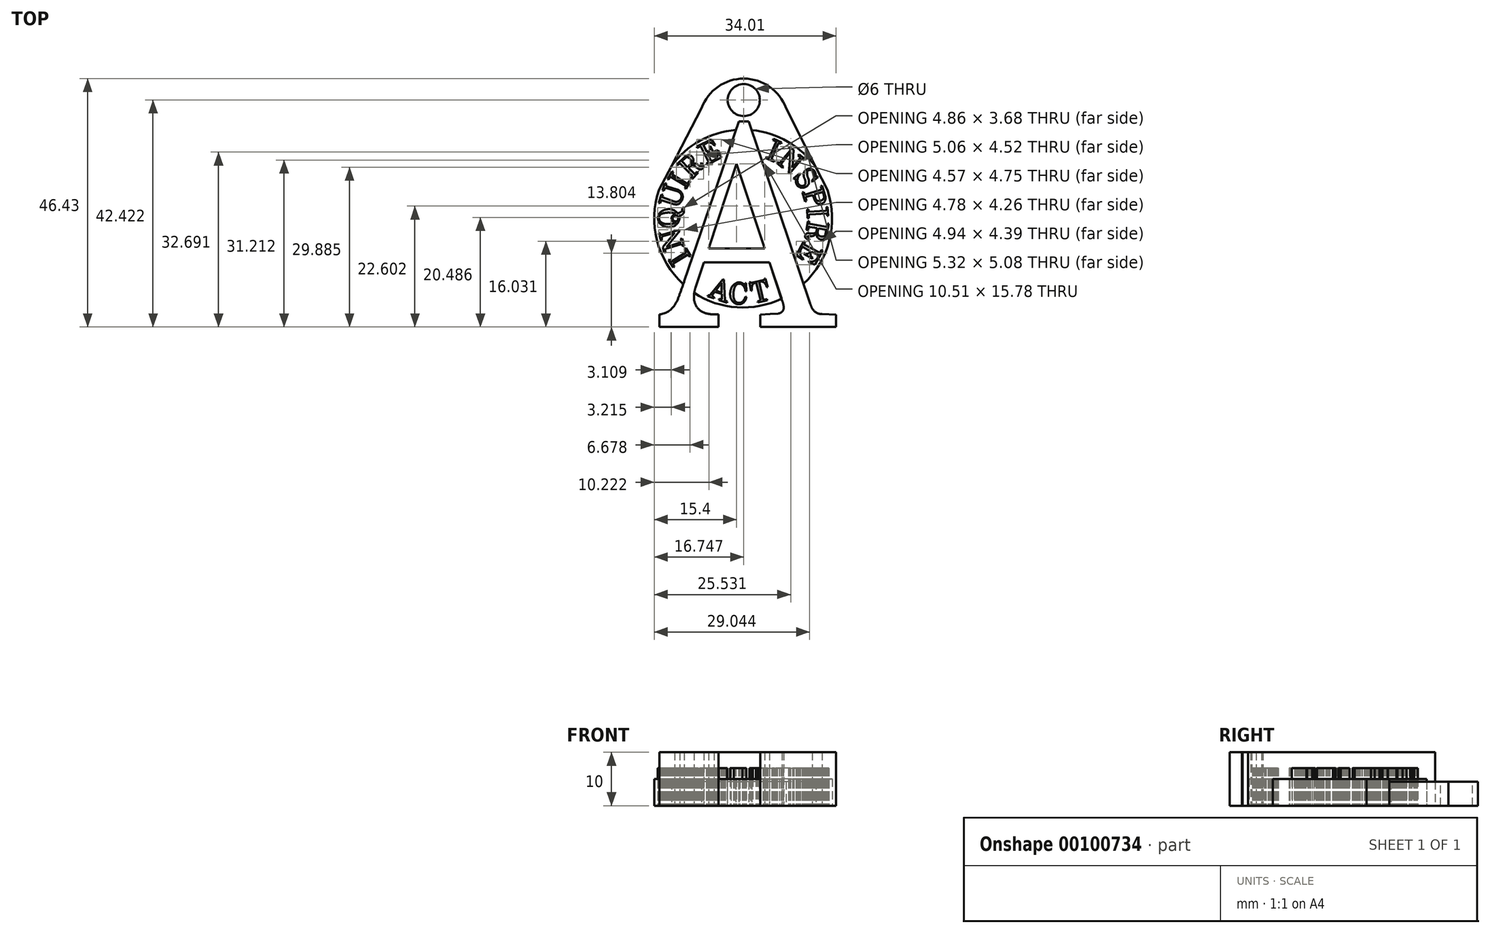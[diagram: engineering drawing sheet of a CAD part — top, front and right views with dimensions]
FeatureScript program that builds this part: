
annotation { "Feature Type Name" : "Feature", "Feature Type Description" : "" }
export const myFeature = defineFeature(function(context is Context, id is Id, definition is map)
    precondition{}
    {
        {
            var Q0;
            Q0=qCreatedBy(makeId("Top.planeOp"),FACE);
            var sketch = newSketch(context, id + "F0", { "sketchPlane" : qUnion([Q0])});
            skArc(sketch, "E0", {"start": v(10.29, 4.86) * mm, "mid": v(11.9, 5.41) * mm, "end": v(13.09, 6.61) * mm});
            skArc(sketch, "E1", {"start": v(13.09, 6.61) * mm, "mid": v(13.66, 7.63) * mm, "end": v(14.06, 8.74) * mm});
            skArc(sketch, "E2", {"start": v(14.06, 8.74) * mm, "mid": v(14.51, 9.92) * mm, "end": v(14.91, 11.11) * mm});
            skLineSegment(sketch, "E3", {"start": v(14.91, 11.11) * mm, "end": v(25.1, 40.93) * mm});
            skLineSegment(sketch, "E4", {"start": v(25.1, 40.93) * mm, "end": v(26.97, 40.93) * mm});
            skLineSegment(sketch, "E5", {"start": v(26.97, 40.93) * mm, "end": v(38.45, 6.88) * mm});
            skArc(sketch, "E6", {"start": v(38.45, 6.88) * mm, "mid": v(38.63, 6.4) * mm, "end": v(38.85, 5.93) * mm});
            skArc(sketch, "E7", {"start": v(38.85, 5.93) * mm, "mid": v(39.62, 5.19) * mm, "end": v(40.67, 4.95) * mm});
            skLineSegment(sketch, "E8", {"start": v(40.67, 4.95) * mm, "end": v(43.3, 4.83) * mm});
            skLineSegment(sketch, "E9", {"start": v(43.3, 4.83) * mm, "end": v(43.3, 2.52) * mm});
            skLineSegment(sketch, "E10", {"start": v(43.3, 2.52) * mm, "end": v(29.1, 2.52) * mm});
            skLineSegment(sketch, "E11", {"start": v(29.1, 2.52) * mm, "end": v(29.1, 4.8) * mm});
            skLineSegment(sketch, "E12", {"start": v(29.1, 4.8) * mm, "end": v(30.97, 4.92) * mm});
            skLineSegment(sketch, "E13", {"start": v(30.97, 4.92) * mm, "end": v(32.48, 5.03) * mm});
            skArc(sketch, "E14", {"start": v(32.48, 5.03) * mm, "mid": v(33.31, 5.5) * mm, "end": v(33.47, 6.45) * mm});
            skArc(sketch, "E15", {"start": v(33.47, 6.45) * mm, "mid": v(33.37, 6.96) * mm, "end": v(33.2, 7.45) * mm});
            skLineSegment(sketch, "E16", {"start": v(33.2, 7.45) * mm, "end": v(30.83, 14.6) * mm});
            skLineSegment(sketch, "E17", {"start": v(30.83, 14.6) * mm, "end": v(18.59, 14.6) * mm});
            skLineSegment(sketch, "E18", {"start": v(18.59, 14.6) * mm, "end": v(17, 9.85) * mm});
            skArc(sketch, "E19", {"start": v(17, 9.85) * mm, "mid": v(16.82, 9.18) * mm, "end": v(16.73, 8.5) * mm});
            skArc(sketch, "E20", {"start": v(16.73, 8.5) * mm, "mid": v(16.76, 7.5) * mm, "end": v(17.08, 6.57) * mm});
            skArc(sketch, "E21", {"start": v(17.08, 6.57) * mm, "mid": v(17.68, 5.76) * mm, "end": v(18.54, 5.22) * mm});
            skArc(sketch, "E22", {"start": v(18.54, 5.22) * mm, "mid": v(19.48, 4.96) * mm, "end": v(20.46, 4.89) * mm});
            skLineSegment(sketch, "E23", {"start": v(20.46, 4.89) * mm, "end": v(21.34, 4.89) * mm});
            skLineSegment(sketch, "E24", {"start": v(21.34, 4.89) * mm, "end": v(21.34, 2.53) * mm});
            skLineSegment(sketch, "E25", {"start": v(21.34, 2.53) * mm, "end": v(10.35, 2.53) * mm});
            skLineSegment(sketch, "E26", {"start": v(10.29, 4.86) * mm, "end": v(10.29, 2.53) * mm});
            skLineSegment(sketch, "E27", {"start": v(10.35, 2.53) * mm, "end": v(10.29, 2.53) * mm});
            skLineSegment(sketch, "E28", {"start": v(24.67, 33.01) * mm, "end": v(29.94, 17.23) * mm});
            skLineSegment(sketch, "E29", {"start": v(29.94, 17.23) * mm, "end": v(19.44, 17.23) * mm});
            skLineSegment(sketch, "E30", {"start": v(19.44, 17.23) * mm, "end": v(24.67, 33.01) * mm});
            skArc(sketch, "E31", {"start": v(37.2, 10.58) * mm, "mid": v(42.03, 18.67) * mm, "end": v(41.68, 28.1) * mm});
            skArc(sketch, "E32", {"start": v(35.3, 16.2) * mm, "mid": v(36.84, 26.47) * mm, "end": v(29.4, 33.72) * mm});
            skArc(sketch, "E33", {"start": v(18.4, 14.04) * mm, "mid": v(24.72, 11.3) * mm, "end": v(31.45, 12.72) * mm});
            skArc(sketch, "E34", {"start": v(16.77, 8.85) * mm, "mid": v(24.8, 6.2) * mm, "end": v(33.09, 7.8) * mm});
            skArc(sketch, "E35", {"start": v(24.56, 39.34) * mm, "mid": v(17.81, 37.3) * mm, "end": v(12.52, 32.65) * mm});
            skArc(sketch, "E36", {"start": v(22.68, 33.84) * mm, "mid": v(15.04, 26.6) * mm, "end": v(16.65, 16.2) * mm});
            skLineSegment(sketch, "E37", {"start": v(22.52, 7.58) * mm, "end": v(22.33, 11.37) * mm});
            skLineSegment(sketch, "E38", {"start": v(22.33, 11.37) * mm, "end": v(22.12, 11.42) * mm});
            skLineSegment(sketch, "E39", {"start": v(22.12, 11.42) * mm, "end": v(19.81, 8.58) * mm});
            skArc(sketch, "E40", {"start": v(19.36, 8.44) * mm, "mid": v(19.61, 8.44) * mm, "end": v(19.81, 8.58) * mm});
            skLineSegment(sketch, "E41", {"start": v(19.36, 8.44) * mm, "end": v(19.3, 8.26) * mm});
            skLineSegment(sketch, "E42", {"start": v(19.3, 8.26) * mm, "end": v(20.5, 7.86) * mm});
            skLineSegment(sketch, "E43", {"start": v(20.5, 7.86) * mm, "end": v(20.55, 8.04) * mm});
            skArc(sketch, "E44", {"start": v(20.23, 8.64) * mm, "mid": v(20.24, 8.25) * mm, "end": v(20.55, 8.04) * mm});
            skLineSegment(sketch, "E45", {"start": v(20.23, 8.64) * mm, "end": v(20.6, 9.1) * mm});
            skLineSegment(sketch, "E46", {"start": v(20.6, 9.1) * mm, "end": v(21.93, 8.68) * mm});
            skLineSegment(sketch, "E47", {"start": v(21.93, 8.68) * mm, "end": v(21.93, 7.8) * mm});
            skArc(sketch, "E48", {"start": v(21.9, 7.7) * mm, "mid": v(21.92, 7.75) * mm, "end": v(21.93, 7.8) * mm});
            skArc(sketch, "E49", {"start": v(21.79, 7.67) * mm, "mid": v(21.84, 7.67) * mm, "end": v(21.9, 7.7) * mm});
            skLineSegment(sketch, "E50", {"start": v(21.79, 7.67) * mm, "end": v(21.43, 7.79) * mm});
            skLineSegment(sketch, "E51", {"start": v(21.43, 7.79) * mm, "end": v(21.36, 7.57) * mm});
            skLineSegment(sketch, "E52", {"start": v(21.36, 7.57) * mm, "end": v(22.88, 7.07) * mm});
            skLineSegment(sketch, "E53", {"start": v(22.88, 7.07) * mm, "end": v(22.95, 7.28) * mm});
            skLineSegment(sketch, "E54", {"start": v(22.95, 7.28) * mm, "end": v(22.6, 7.39) * mm});
            skArc(sketch, "E55", {"start": v(22.52, 7.58) * mm, "mid": v(22.54, 7.47) * mm, "end": v(22.6, 7.39) * mm});
            skLineSegment(sketch, "E56", {"start": v(20.78, 9.33) * mm, "end": v(21.88, 8.97) * mm});
            skLineSegment(sketch, "E57", {"start": v(21.88, 8.97) * mm, "end": v(21.88, 10.76) * mm});
            skLineSegment(sketch, "E58", {"start": v(21.88, 10.76) * mm, "end": v(20.78, 9.33) * mm});
            skArc(sketch, "E59", {"start": v(26.12, 10.42) * mm, "mid": v(25.76, 10.71) * mm, "end": v(25.31, 10.84) * mm});
            skArc(sketch, "E60", {"start": v(25.31, 10.84) * mm, "mid": v(24.93, 10.83) * mm, "end": v(24.58, 10.69) * mm});
            skArc(sketch, "E61", {"start": v(24.58, 10.69) * mm, "mid": v(24.03, 10.28) * mm, "end": v(23.67, 9.7) * mm});
            skArc(sketch, "E62", {"start": v(23.67, 9.7) * mm, "mid": v(23.5, 8.89) * mm, "end": v(23.55, 8.06) * mm});
            skArc(sketch, "E63", {"start": v(23.55, 8.06) * mm, "mid": v(23.78, 7.55) * mm, "end": v(24.15, 7.12) * mm});
            skArc(sketch, "E64", {"start": v(24.15, 7.12) * mm, "mid": v(24.5, 6.9) * mm, "end": v(24.89, 6.77) * mm});
            skArc(sketch, "E65", {"start": v(24.89, 6.77) * mm, "mid": v(25.32, 6.78) * mm, "end": v(25.73, 6.91) * mm});
            skArc(sketch, "E66", {"start": v(25.73, 6.91) * mm, "mid": v(26.28, 7.41) * mm, "end": v(26.51, 8.12) * mm});
            skLineSegment(sketch, "E67", {"start": v(26.51, 8.12) * mm, "end": v(26.33, 8.17) * mm});
            skArc(sketch, "E68", {"start": v(25.76, 7.21) * mm, "mid": v(26.11, 7.65) * mm, "end": v(26.33, 8.17) * mm});
            skArc(sketch, "E69", {"start": v(24.3, 7.52) * mm, "mid": v(24.96, 7.03) * mm, "end": v(25.76, 7.21) * mm});
            skArc(sketch, "E70", {"start": v(24.1, 8.38) * mm, "mid": v(24.15, 7.94) * mm, "end": v(24.3, 7.52) * mm});
            skLineSegment(sketch, "E71", {"start": v(24.1, 8.38) * mm, "end": v(24.13, 9.08) * mm});
            skArc(sketch, "E72", {"start": v(24.55, 10.3) * mm, "mid": v(24.25, 9.71) * mm, "end": v(24.13, 9.08) * mm});
            skArc(sketch, "E73", {"start": v(25.06, 10.6) * mm, "mid": v(24.78, 10.5) * mm, "end": v(24.55, 10.3) * mm});
            skArc(sketch, "E74", {"start": v(26, 10.15) * mm, "mid": v(25.6, 10.53) * mm, "end": v(25.06, 10.6) * mm});
            skArc(sketch, "E75", {"start": v(26.34, 9.19) * mm, "mid": v(26.24, 9.7) * mm, "end": v(26, 10.14) * mm});
            skLineSegment(sketch, "E76", {"start": v(26.34, 9.19) * mm, "end": v(26.54, 9.19) * mm});
            skLineSegment(sketch, "E77", {"start": v(26.54, 9.19) * mm, "end": v(26.48, 10.73) * mm});
            skLineSegment(sketch, "E78", {"start": v(26.48, 10.73) * mm, "end": v(26.3, 10.72) * mm});
            skLineSegment(sketch, "E79", {"start": v(26.3, 10.72) * mm, "end": v(26.17, 10.38) * mm});
            skLineSegment(sketch, "E80", {"start": v(26.17, 10.38) * mm, "end": v(26.12, 10.42) * mm});
            skLineSegment(sketch, "E81", {"start": v(27.38, 9.27) * mm, "end": v(27.1, 10.87) * mm});
            skLineSegment(sketch, "E82", {"start": v(27.1, 10.87) * mm, "end": v(27.27, 10.9) * mm});
            skLineSegment(sketch, "E83", {"start": v(27.38, 9.27) * mm, "end": v(27.55, 9.3) * mm});
            skArc(sketch, "E84", {"start": v(27.7, 10.47) * mm, "mid": v(27.53, 9.9) * mm, "end": v(27.55, 9.3) * mm});
            skArc(sketch, "E85", {"start": v(28.3, 10.8) * mm, "mid": v(27.97, 10.7) * mm, "end": v(27.7, 10.47) * mm});
            skArc(sketch, "E86", {"start": v(28.45, 10.61) * mm, "mid": v(28.4, 10.72) * mm, "end": v(28.3, 10.8) * mm});
            skLineSegment(sketch, "E87", {"start": v(28.45, 10.61) * mm, "end": v(29.16, 7.48) * mm});
            skLineSegment(sketch, "E88", {"start": v(29.16, 7.48) * mm, "end": v(28.64, 7.31) * mm});
            skLineSegment(sketch, "E89", {"start": v(28.64, 7.31) * mm, "end": v(28.7, 7.08) * mm});
            skLineSegment(sketch, "E90", {"start": v(28.7, 7.08) * mm, "end": v(30.41, 7.5) * mm});
            skLineSegment(sketch, "E91", {"start": v(30.41, 7.5) * mm, "end": v(30.36, 7.7) * mm});
            skLineSegment(sketch, "E92", {"start": v(30.36, 7.7) * mm, "end": v(29.89, 7.62) * mm});
            skArc(sketch, "E93", {"start": v(29.72, 7.62) * mm, "mid": v(29.8, 7.61) * mm, "end": v(29.89, 7.62) * mm});
            skArc(sketch, "E94", {"start": v(29.64, 7.72) * mm, "mid": v(29.67, 7.66) * mm, "end": v(29.72, 7.62) * mm});
            skLineSegment(sketch, "E95", {"start": v(29.64, 7.72) * mm, "end": v(28.95, 10.83) * mm});
            skArc(sketch, "E96", {"start": v(29.17, 11) * mm, "mid": v(29.03, 10.96) * mm, "end": v(28.95, 10.83) * mm});
            skArc(sketch, "E97", {"start": v(29.87, 10.78) * mm, "mid": v(29.55, 10.98) * mm, "end": v(29.17, 11) * mm});
            skArc(sketch, "E98", {"start": v(30.32, 9.94) * mm, "mid": v(30.15, 10.39) * mm, "end": v(29.87, 10.78) * mm});
            skLineSegment(sketch, "E99", {"start": v(30.32, 9.94) * mm, "end": v(30.5, 9.98) * mm});
            skLineSegment(sketch, "E100", {"start": v(30.5, 9.98) * mm, "end": v(30.07, 11.56) * mm});
            skLineSegment(sketch, "E101", {"start": v(30.07, 11.56) * mm, "end": v(29.9, 11.54) * mm});
            skArc(sketch, "E102", {"start": v(29.73, 11.3) * mm, "mid": v(29.86, 11.4) * mm, "end": v(29.9, 11.54) * mm});
            skArc(sketch, "E103", {"start": v(27.27, 10.9) * mm, "mid": v(27.38, 10.8) * mm, "end": v(27.53, 10.8) * mm});
            skLineSegment(sketch, "E104", {"start": v(27.53, 10.8) * mm, "end": v(29.73, 11.3) * mm});
            skLineSegment(sketch, "E105", {"start": v(31.59, 37.68) * mm, "end": v(33.11, 37) * mm});
            skLineSegment(sketch, "E106", {"start": v(33.11, 37) * mm, "end": v(33, 36.77) * mm});
            skLineSegment(sketch, "E107", {"start": v(31.59, 37.68) * mm, "end": v(31.49, 37.46) * mm});
            skLineSegment(sketch, "E108", {"start": v(31.49, 37.46) * mm, "end": v(31.92, 37.27) * mm});
            skLineSegment(sketch, "E109", {"start": v(30.16, 34.07) * mm, "end": v(31.7, 33.38) * mm});
            skLineSegment(sketch, "E110", {"start": v(31.7, 33.38) * mm, "end": v(31.78, 33.58) * mm});
            skLineSegment(sketch, "E111", {"start": v(30.16, 34.07) * mm, "end": v(30.25, 34.27) * mm});
            skLineSegment(sketch, "E112", {"start": v(31.29, 34.1) * mm, "end": v(32.52, 36.85) * mm});
            skLineSegment(sketch, "E113", {"start": v(30.25, 34.27) * mm, "end": v(30.57, 34.12) * mm});
            skLineSegment(sketch, "E114", {"start": v(31.78, 33.58) * mm, "end": v(31.31, 33.81) * mm});
            skLineSegment(sketch, "E115", {"start": v(30.8, 34.26) * mm, "end": v(32.06, 37) * mm});
            skLineSegment(sketch, "E116", {"start": v(31.92, 37.27) * mm, "end": v(31.98, 37.24) * mm});
            skLineSegment(sketch, "E117", {"start": v(33, 36.77) * mm, "end": v(32.64, 36.93) * mm});
            skArc(sketch, "E118", {"start": v(32.64, 36.93) * mm, "mid": v(32.57, 36.9) * mm, "end": v(32.52, 36.85) * mm});
            skArc(sketch, "E119", {"start": v(32.06, 37) * mm, "mid": v(32.07, 37.14) * mm, "end": v(31.98, 37.24) * mm});
            skArc(sketch, "E120", {"start": v(30.57, 34.12) * mm, "mid": v(30.73, 34.13) * mm, "end": v(30.8, 34.26) * mm});
            skArc(sketch, "E121", {"start": v(31.29, 34.1) * mm, "mid": v(31.27, 33.95) * mm, "end": v(31.31, 33.81) * mm});
            skLineSegment(sketch, "E122", {"start": v(34.72, 35.52) * mm, "end": v(32.83, 33.3) * mm});
            skLineSegment(sketch, "E123", {"start": v(34.78, 35.23) * mm, "end": v(33.12, 33.14) * mm});
            skLineSegment(sketch, "E124", {"start": v(33.44, 32.46) * mm, "end": v(33.14, 32.78) * mm});
            skLineSegment(sketch, "E125", {"start": v(33.44, 32.46) * mm, "end": v(33.3, 32.26) * mm});
            skLineSegment(sketch, "E126", {"start": v(33.3, 32.26) * mm, "end": v(32.16, 33.2) * mm});
            skLineSegment(sketch, "E127", {"start": v(32.16, 33.2) * mm, "end": v(32.31, 33.4) * mm});
            skLineSegment(sketch, "E128", {"start": v(32.31, 33.4) * mm, "end": v(32.49, 33.26) * mm});
            skLineSegment(sketch, "E129", {"start": v(34.65, 35.86) * mm, "end": v(34.38, 36.1) * mm});
            skLineSegment(sketch, "E130", {"start": v(34.38, 36.1) * mm, "end": v(34.53, 36.27) * mm});
            skLineSegment(sketch, "E131", {"start": v(34.53, 36.27) * mm, "end": v(35.32, 35.62) * mm});
            skLineSegment(sketch, "E132", {"start": v(35.32, 35.62) * mm, "end": v(35.12, 32.3) * mm});
            skLineSegment(sketch, "E133", {"start": v(35.12, 32.3) * mm, "end": v(36.45, 33.9) * mm});
            skLineSegment(sketch, "E134", {"start": v(36.45, 34.35) * mm, "end": v(36.19, 34.62) * mm});
            skLineSegment(sketch, "E135", {"start": v(36.19, 34.62) * mm, "end": v(36.34, 34.8) * mm});
            skLineSegment(sketch, "E136", {"start": v(36.34, 34.8) * mm, "end": v(37.48, 33.89) * mm});
            skLineSegment(sketch, "E137", {"start": v(37.48, 33.89) * mm, "end": v(37.31, 33.68) * mm});
            skLineSegment(sketch, "E138", {"start": v(37.31, 33.68) * mm, "end": v(37.18, 33.8) * mm});
            skLineSegment(sketch, "E139", {"start": v(36.74, 33.77) * mm, "end": v(34.6, 31.19) * mm});
            skLineSegment(sketch, "E140", {"start": v(34.6, 31.19) * mm, "end": v(34.43, 31.31) * mm});
            skLineSegment(sketch, "E141", {"start": v(34.43, 31.31) * mm, "end": v(34.78, 35.23) * mm});
            skArc(sketch, "E142", {"start": v(33.12, 33.14) * mm, "mid": v(33.06, 32.96) * mm, "end": v(33.14, 32.78) * mm});
            skArc(sketch, "E143", {"start": v(32.49, 33.26) * mm, "mid": v(32.67, 33.2) * mm, "end": v(32.83, 33.3) * mm});
            skArc(sketch, "E144", {"start": v(34.72, 35.52) * mm, "mid": v(34.74, 35.7) * mm, "end": v(34.65, 35.86) * mm});
            skArc(sketch, "E145", {"start": v(36.45, 33.9) * mm, "mid": v(36.53, 34.12) * mm, "end": v(36.45, 34.35) * mm});
            skArc(sketch, "E146", {"start": v(37.18, 33.8) * mm, "mid": v(36.96, 33.87) * mm, "end": v(36.74, 33.77) * mm});
            skLineSegment(sketch, "E147", {"start": v(38.82, 29.64) * mm, "end": v(39.92, 30.53) * mm});
            skLineSegment(sketch, "E148", {"start": v(39.92, 30.53) * mm, "end": v(39.82, 30.65) * mm});
            skLineSegment(sketch, "E149", {"start": v(39.82, 30.65) * mm, "end": v(39.47, 30.65) * mm});
            skLineSegment(sketch, "E150", {"start": v(38.82, 29.64) * mm, "end": v(38.7, 29.78) * mm});
            skLineSegment(sketch, "E151", {"start": v(38.7, 29.78) * mm, "end": v(38.9, 30.03) * mm});
            skLineSegment(sketch, "E152", {"start": v(39.47, 30.65) * mm, "end": v(39.47, 31.12) * mm});
            skLineSegment(sketch, "E153", {"start": v(35.31, 30.31) * mm, "end": v(36.5, 31.25) * mm});
            skLineSegment(sketch, "E154", {"start": v(36.5, 31.25) * mm, "end": v(36.61, 31.1) * mm});
            skLineSegment(sketch, "E155", {"start": v(35.31, 30.31) * mm, "end": v(35.41, 30.18) * mm});
            skLineSegment(sketch, "E156", {"start": v(35.41, 30.18) * mm, "end": v(35.8, 30.2) * mm});
            skLineSegment(sketch, "E157", {"start": v(35.8, 30.2) * mm, "end": v(35.78, 29.74) * mm});
            skArc(sketch, "E158", {"start": v(36.61, 31.1) * mm, "mid": v(36.13, 30.37) * mm, "end": v(36.12, 29.5) * mm});
            skArc(sketch, "E159", {"start": v(35.78, 29.74) * mm, "mid": v(35.99, 29.05) * mm, "end": v(36.57, 28.62) * mm});
            skArc(sketch, "E160", {"start": v(36.57, 28.62) * mm, "mid": v(37.3, 28.58) * mm, "end": v(37.94, 28.94) * mm});
            skArc(sketch, "E161", {"start": v(37.94, 28.94) * mm, "mid": v(38.16, 29.24) * mm, "end": v(38.22, 29.6) * mm});
            skArc(sketch, "E162", {"start": v(38.22, 29.6) * mm, "mid": v(38.18, 30) * mm, "end": v(38.06, 30.39) * mm});
            skArc(sketch, "E163", {"start": v(37.85, 31.37) * mm, "mid": v(37.9, 30.87) * mm, "end": v(38.06, 30.39) * mm});
            skArc(sketch, "E164", {"start": v(38.2, 31.83) * mm, "mid": v(37.96, 31.65) * mm, "end": v(37.85, 31.37) * mm});
            skArc(sketch, "E165", {"start": v(39.08, 31.45) * mm, "mid": v(38.72, 31.83) * mm, "end": v(38.2, 31.83) * mm});
            skArc(sketch, "E166", {"start": v(38.9, 30.03) * mm, "mid": v(39.23, 30.71) * mm, "end": v(39.08, 31.45) * mm});
            skArc(sketch, "E167", {"start": v(39.47, 31.12) * mm, "mid": v(39.24, 31.66) * mm, "end": v(38.77, 32.03) * mm});
            skArc(sketch, "E168", {"start": v(38.77, 32.03) * mm, "mid": v(38.2, 32.11) * mm, "end": v(37.69, 31.88) * mm});
            skArc(sketch, "E169", {"start": v(37.69, 31.88) * mm, "mid": v(37.34, 31.57) * mm, "end": v(37.21, 31.12) * mm});
            skArc(sketch, "E170", {"start": v(37.21, 31.12) * mm, "mid": v(37.26, 30.67) * mm, "end": v(37.41, 30.25) * mm});
            skArc(sketch, "E171", {"start": v(37.52, 29.19) * mm, "mid": v(37.56, 29.73) * mm, "end": v(37.41, 30.25) * mm});
            skArc(sketch, "E172", {"start": v(36.94, 28.87) * mm, "mid": v(37.27, 28.96) * mm, "end": v(37.52, 29.19) * mm});
            skArc(sketch, "E173", {"start": v(36.12, 29.5) * mm, "mid": v(36.43, 29.05) * mm, "end": v(36.94, 28.87) * mm});
            skLineSegment(sketch, "E174", {"start": v(37.42, 27.25) * mm, "end": v(40.51, 28.2) * mm});
            skLineSegment(sketch, "E175", {"start": v(37.42, 27.25) * mm, "end": v(37.27, 27.73) * mm});
            skLineSegment(sketch, "E176", {"start": v(37.27, 27.73) * mm, "end": v(36.98, 27.65) * mm});
            skLineSegment(sketch, "E177", {"start": v(36.98, 27.65) * mm, "end": v(37.5, 25.98) * mm});
            skLineSegment(sketch, "E178", {"start": v(37.5, 25.98) * mm, "end": v(37.76, 26.06) * mm});
            skLineSegment(sketch, "E179", {"start": v(37.76, 26.06) * mm, "end": v(37.62, 26.54) * mm});
            skLineSegment(sketch, "E180", {"start": v(37.71, 26.82) * mm, "end": v(39, 27.19) * mm});
            skLineSegment(sketch, "E181", {"start": v(39, 27.19) * mm, "end": v(39.2, 26.47) * mm});
            skLineSegment(sketch, "E182", {"start": v(39.24, 27.27) * mm, "end": v(40.8, 27.71) * mm});
            skLineSegment(sketch, "E183", {"start": v(40.8, 27.71) * mm, "end": v(40.97, 27.21) * mm});
            skLineSegment(sketch, "E184", {"start": v(39.24, 27.27) * mm, "end": v(39.43, 26.6) * mm});
            skLineSegment(sketch, "E185", {"start": v(40.56, 28.45) * mm, "end": v(40.44, 28.85) * mm});
            skLineSegment(sketch, "E186", {"start": v(40.44, 28.85) * mm, "end": v(40.7, 28.94) * mm});
            skLineSegment(sketch, "E187", {"start": v(40.7, 28.94) * mm, "end": v(41.27, 27.01) * mm});
            skArc(sketch, "E188", {"start": v(39.43, 26.6) * mm, "mid": v(39.57, 26.3) * mm, "end": v(39.8, 26.08) * mm});
            skArc(sketch, "E189", {"start": v(39.8, 26.08) * mm, "mid": v(40.47, 26.13) * mm, "end": v(41, 26.54) * mm});
            skArc(sketch, "E190", {"start": v(41, 26.54) * mm, "mid": v(41.03, 26.88) * mm, "end": v(40.97, 27.21) * mm});
            skArc(sketch, "E191", {"start": v(41.09, 25.9) * mm, "mid": v(41.3, 26.43) * mm, "end": v(41.27, 27.01) * mm});
            skArc(sketch, "E192", {"start": v(40.32, 25.5) * mm, "mid": v(40.74, 25.61) * mm, "end": v(41.09, 25.9) * mm});
            skArc(sketch, "E193", {"start": v(39.5, 25.89) * mm, "mid": v(39.85, 25.56) * mm, "end": v(40.32, 25.5) * mm});
            skArc(sketch, "E194", {"start": v(39.2, 26.47) * mm, "mid": v(39.32, 26.16) * mm, "end": v(39.5, 25.89) * mm});
            skArc(sketch, "E195", {"start": v(40.51, 28.2) * mm, "mid": v(40.58, 28.31) * mm, "end": v(40.56, 28.45) * mm});
            skArc(sketch, "E196", {"start": v(37.71, 26.82) * mm, "mid": v(37.62, 26.7) * mm, "end": v(37.62, 26.54) * mm});
            skLineSegment(sketch, "E197", {"start": v(41.83, 23.28) * mm, "end": v(41.71, 24.93) * mm});
            skLineSegment(sketch, "E198", {"start": v(41.71, 24.93) * mm, "end": v(41.48, 24.94) * mm});
            skLineSegment(sketch, "E199", {"start": v(41.48, 24.94) * mm, "end": v(41.5, 24.46) * mm});
            skLineSegment(sketch, "E200", {"start": v(41.83, 23.28) * mm, "end": v(41.6, 23.27) * mm});
            skLineSegment(sketch, "E201", {"start": v(41.6, 23.27) * mm, "end": v(41.55, 23.75) * mm});
            skLineSegment(sketch, "E202", {"start": v(41.55, 23.75) * mm, "end": v(38.38, 23.52) * mm});
            skLineSegment(sketch, "E203", {"start": v(38.22, 23.34) * mm, "end": v(38.22, 22.84) * mm});
            skLineSegment(sketch, "E204", {"start": v(38.22, 22.84) * mm, "end": v(37.96, 22.82) * mm});
            skLineSegment(sketch, "E205", {"start": v(37.96, 22.82) * mm, "end": v(37.86, 24.49) * mm});
            skLineSegment(sketch, "E206", {"start": v(37.86, 24.49) * mm, "end": v(38.1, 24.5) * mm});
            skLineSegment(sketch, "E207", {"start": v(38.1, 24.5) * mm, "end": v(38.12, 24.04) * mm});
            skLineSegment(sketch, "E208", {"start": v(38.12, 24.04) * mm, "end": v(41.31, 24.26) * mm});
            skArc(sketch, "E209", {"start": v(41.31, 24.26) * mm, "mid": v(41.44, 24.32) * mm, "end": v(41.5, 24.46) * mm});
            skArc(sketch, "E210", {"start": v(38.38, 23.52) * mm, "mid": v(38.26, 23.46) * mm, "end": v(38.22, 23.34) * mm});
            skLineSegment(sketch, "E211", {"start": v(38.23, 21.81) * mm, "end": v(41.28, 21.27) * mm});
            skLineSegment(sketch, "E212", {"start": v(41.57, 21.39) * mm, "end": v(41.68, 21.87) * mm});
            skLineSegment(sketch, "E213", {"start": v(41.68, 21.87) * mm, "end": v(41.92, 21.82) * mm});
            skLineSegment(sketch, "E214", {"start": v(41.92, 21.82) * mm, "end": v(41.51, 19.64) * mm});
            skLineSegment(sketch, "E215", {"start": v(41.32, 19.93) * mm, "end": v(41.46, 20.68) * mm});
            skLineSegment(sketch, "E216", {"start": v(41.46, 20.68) * mm, "end": v(39.98, 20.95) * mm});
            skLineSegment(sketch, "E217", {"start": v(39.98, 20.95) * mm, "end": v(39.88, 20.4) * mm});
            skLineSegment(sketch, "E218", {"start": v(39.63, 20.47) * mm, "end": v(39.74, 21) * mm});
            skLineSegment(sketch, "E219", {"start": v(39.74, 21) * mm, "end": v(38.38, 21.23) * mm});
            skLineSegment(sketch, "E220", {"start": v(38.07, 21.09) * mm, "end": v(37.99, 20.63) * mm});
            skLineSegment(sketch, "E221", {"start": v(37.99, 20.63) * mm, "end": v(37.75, 20.68) * mm});
            skLineSegment(sketch, "E222", {"start": v(37.75, 20.68) * mm, "end": v(38.03, 22.3) * mm});
            skLineSegment(sketch, "E223", {"start": v(38.03, 22.3) * mm, "end": v(38.29, 22.27) * mm});
            skLineSegment(sketch, "E224", {"start": v(38.29, 22.27) * mm, "end": v(38.23, 21.81) * mm});
            skArc(sketch, "E225", {"start": v(38.38, 21.23) * mm, "mid": v(38.19, 21.23) * mm, "end": v(38.07, 21.09) * mm});
            skArc(sketch, "E226", {"start": v(41.28, 21.27) * mm, "mid": v(41.46, 21.25) * mm, "end": v(41.57, 21.39) * mm});
            skArc(sketch, "E227", {"start": v(39.88, 20.4) * mm, "mid": v(39.88, 20.04) * mm, "end": v(39.97, 19.7) * mm});
            skArc(sketch, "E228", {"start": v(40.78, 19.43) * mm, "mid": v(41.16, 19.57) * mm, "end": v(41.32, 19.93) * mm});
            skArc(sketch, "E229", {"start": v(39.97, 19.7) * mm, "mid": v(40.34, 19.46) * mm, "end": v(40.78, 19.43) * mm});
            skArc(sketch, "E230", {"start": v(40.68, 18.84) * mm, "mid": v(41.22, 19.1) * mm, "end": v(41.51, 19.64) * mm});
            skArc(sketch, "E231", {"start": v(39.72, 19.47) * mm, "mid": v(40.1, 18.99) * mm, "end": v(40.68, 18.84) * mm});
            skArc(sketch, "E232", {"start": v(39.66, 20.06) * mm, "mid": v(39.67, 19.76) * mm, "end": v(39.72, 19.47) * mm});
            skArc(sketch, "E233", {"start": v(37.85, 19.22) * mm, "mid": v(38.07, 19.06) * mm, "end": v(38.32, 19) * mm});
            skArc(sketch, "E234", {"start": v(38.06, 19.45) * mm, "mid": v(37.9, 19.38) * mm, "end": v(37.85, 19.22) * mm});
            skArc(sketch, "E235", {"start": v(38.62, 19.5) * mm, "mid": v(38.34, 19.49) * mm, "end": v(38.06, 19.45) * mm});
            skArc(sketch, "E236", {"start": v(38.62, 19.5) * mm, "mid": v(38.92, 19.53) * mm, "end": v(39.2, 19.64) * mm});
            skArc(sketch, "E237", {"start": v(39.2, 19.64) * mm, "mid": v(39.47, 19.8) * mm, "end": v(39.66, 20.06) * mm});
            skLineSegment(sketch, "E238", {"start": v(38.32, 19) * mm, "end": v(38.32, 18.83) * mm});
            skArc(sketch, "E239", {"start": v(37.52, 19.3) * mm, "mid": v(37.86, 18.96) * mm, "end": v(38.32, 18.83) * mm});
            skArc(sketch, "E240", {"start": v(38.03, 20.04) * mm, "mid": v(37.6, 19.79) * mm, "end": v(37.52, 19.3) * mm});
            skLineSegment(sketch, "E241", {"start": v(38.03, 20.04) * mm, "end": v(39.08, 20.01) * mm});
            skArc(sketch, "E242", {"start": v(39.08, 20.01) * mm, "mid": v(39.44, 20.14) * mm, "end": v(39.63, 20.47) * mm});
            skLineSegment(sketch, "E243", {"start": v(37.26, 17.96) * mm, "end": v(37.48, 18.41) * mm});
            skLineSegment(sketch, "E244", {"start": v(37.48, 18.41) * mm, "end": v(37.25, 18.52) * mm});
            skLineSegment(sketch, "E245", {"start": v(37.25, 18.52) * mm, "end": v(35.87, 15.9) * mm});
            skLineSegment(sketch, "E246", {"start": v(35.87, 15.9) * mm, "end": v(37.14, 15.09) * mm});
            skLineSegment(sketch, "E247", {"start": v(37.14, 15.09) * mm, "end": v(37.22, 15.27) * mm});
            skLineSegment(sketch, "E248", {"start": v(38.19, 14.83) * mm, "end": v(38.1, 14.64) * mm});
            skLineSegment(sketch, "E249", {"start": v(38.1, 14.64) * mm, "end": v(39.37, 14.13) * mm});
            skLineSegment(sketch, "E250", {"start": v(39.37, 14.13) * mm, "end": v(40.8, 16.85) * mm});
            skLineSegment(sketch, "E251", {"start": v(40.8, 16.85) * mm, "end": v(40.56, 16.97) * mm});
            skLineSegment(sketch, "E252", {"start": v(40.56, 16.97) * mm, "end": v(40.35, 16.57) * mm});
            skLineSegment(sketch, "E253", {"start": v(37.26, 17.96) * mm, "end": v(40.07, 16.48) * mm});
            skLineSegment(sketch, "E254", {"start": v(40.01, 15.9) * mm, "end": v(38.7, 16.6) * mm});
            skLineSegment(sketch, "E255", {"start": v(38.7, 16.6) * mm, "end": v(38.63, 16.47) * mm});
            skLineSegment(sketch, "E256", {"start": v(38.46, 16.71) * mm, "end": v(38.4, 16.6) * mm});
            skLineSegment(sketch, "E257", {"start": v(38.46, 16.71) * mm, "end": v(37.09, 17.44) * mm});
            skArc(sketch, "E258", {"start": v(37.09, 17.44) * mm, "mid": v(36.98, 17.4) * mm, "end": v(36.9, 17.3) * mm});
            skArc(sketch, "E259", {"start": v(37.32, 16.34) * mm, "mid": v(37.93, 16.18) * mm, "end": v(38.4, 16.6) * mm});
            skArc(sketch, "E260", {"start": v(38.63, 16.47) * mm, "mid": v(38.54, 15.9) * mm, "end": v(38.93, 15.49) * mm});
            skArc(sketch, "E261", {"start": v(36.9, 17.3) * mm, "mid": v(36.59, 16.21) * mm, "end": v(37.22, 15.27) * mm});
            skLineSegment(sketch, "E262", {"start": v(39.88, 15.63) * mm, "end": v(40.01, 15.9) * mm});
            skArc(sketch, "E263", {"start": v(38.19, 14.83) * mm, "mid": v(39.22, 14.85) * mm, "end": v(39.88, 15.63) * mm});
            skLineSegment(sketch, "E264", {"start": v(37.32, 16.34) * mm, "end": v(37.22, 16.16) * mm});
            skLineSegment(sketch, "E265", {"start": v(37.22, 16.16) * mm, "end": v(38.85, 15.28) * mm});
            skLineSegment(sketch, "E266", {"start": v(38.85, 15.28) * mm, "end": v(38.93, 15.49) * mm});
            skLineSegment(sketch, "E267", {"start": v(11.96, 15.06) * mm, "end": v(12.85, 13.63) * mm});
            skLineSegment(sketch, "E268", {"start": v(12.85, 13.63) * mm, "end": v(13.07, 13.77) * mm});
            skLineSegment(sketch, "E269", {"start": v(13.07, 13.77) * mm, "end": v(12.8, 14.21) * mm});
            skLineSegment(sketch, "E270", {"start": v(11.96, 15.06) * mm, "end": v(12.16, 15.2) * mm});
            skLineSegment(sketch, "E271", {"start": v(12.16, 15.2) * mm, "end": v(12.48, 14.74) * mm});
            skLineSegment(sketch, "E272", {"start": v(12.48, 14.74) * mm, "end": v(15.2, 16.45) * mm});
            skLineSegment(sketch, "E273", {"start": v(12.85, 14.4) * mm, "end": v(15.6, 16.05) * mm});
            skLineSegment(sketch, "E274", {"start": v(15.6, 16.05) * mm, "end": v(15.84, 15.67) * mm});
            skLineSegment(sketch, "E275", {"start": v(15.84, 15.67) * mm, "end": v(16.07, 15.82) * mm});
            skLineSegment(sketch, "E276", {"start": v(16.07, 15.82) * mm, "end": v(15.2, 17.24) * mm});
            skLineSegment(sketch, "E277", {"start": v(15.2, 17.24) * mm, "end": v(15, 17.12) * mm});
            skLineSegment(sketch, "E278", {"start": v(15, 17.12) * mm, "end": v(15.21, 16.72) * mm});
            skArc(sketch, "E279", {"start": v(12.85, 14.4) * mm, "mid": v(12.78, 14.31) * mm, "end": v(12.8, 14.21) * mm});
            skArc(sketch, "E280", {"start": v(15.2, 16.45) * mm, "mid": v(15.27, 16.58) * mm, "end": v(15.21, 16.72) * mm});
            skArc(sketch, "E281", {"start": v(11.44, 17.16) * mm, "mid": v(11.34, 16.84) * mm, "end": v(11.4, 16.5) * mm});
            skArc(sketch, "E282", {"start": v(14.64, 17.56) * mm, "mid": v(14.48, 17.85) * mm, "end": v(14.18, 17.96) * mm});
            skArc(sketch, "E283", {"start": v(14.1, 18.25) * mm, "mid": v(14.3, 18.58) * mm, "end": v(14.22, 18.96) * mm});
            skArc(sketch, "E284", {"start": v(11.09, 19.56) * mm, "mid": v(10.73, 19.26) * mm, "end": v(10.72, 18.8) * mm});
            skArc(sketch, "E285", {"start": v(10.34, 20.13) * mm, "mid": v(10.57, 19.77) * mm, "end": v(11, 19.81) * mm});
            skLineSegment(sketch, "E286", {"start": v(11.09, 19.56) * mm, "end": v(13.12, 20.12) * mm});
            skLineSegment(sketch, "E287", {"start": v(13.12, 20.12) * mm, "end": v(10.9, 17.44) * mm});
            skLineSegment(sketch, "E288", {"start": v(10.9, 17.44) * mm, "end": v(11.17, 16.42) * mm});
            skLineSegment(sketch, "E289", {"start": v(11.17, 16.42) * mm, "end": v(11.4, 16.5) * mm});
            skLineSegment(sketch, "E290", {"start": v(11.44, 17.16) * mm, "end": v(14.18, 17.96) * mm});
            skLineSegment(sketch, "E291", {"start": v(14.64, 17.56) * mm, "end": v(14.9, 17.63) * mm});
            skLineSegment(sketch, "E292", {"start": v(14.9, 17.63) * mm, "end": v(14.5, 19.05) * mm});
            skLineSegment(sketch, "E293", {"start": v(14.5, 19.05) * mm, "end": v(14.22, 18.96) * mm});
            skLineSegment(sketch, "E294", {"start": v(14.1, 18.25) * mm, "end": v(11.62, 17.47) * mm});
            skLineSegment(sketch, "E295", {"start": v(11.62, 17.47) * mm, "end": v(14.09, 20.48) * mm});
            skLineSegment(sketch, "E296", {"start": v(14.09, 20.48) * mm, "end": v(14.03, 20.68) * mm});
            skLineSegment(sketch, "E297", {"start": v(14.03, 20.68) * mm, "end": v(11, 19.81) * mm});
            skLineSegment(sketch, "E298", {"start": v(10.34, 20.13) * mm, "end": v(10.12, 20.07) * mm});
            skLineSegment(sketch, "E299", {"start": v(10.12, 20.07) * mm, "end": v(10.55, 18.67) * mm});
            skLineSegment(sketch, "E300", {"start": v(10.55, 18.67) * mm, "end": v(10.72, 18.8) * mm});
            skLineSegment(sketch, "E301", {"start": v(13.3, 23.36) * mm, "end": v(13.64, 23.36) * mm});
            skLineSegment(sketch, "E302", {"start": v(13.96, 23.38) * mm, "end": v(14.3, 23.38) * mm});
            skArc(sketch, "E303", {"start": v(12.46, 21.2) * mm, "mid": v(13.7, 21.96) * mm, "end": v(13.96, 23.38) * mm});
            skArc(sketch, "E304", {"start": v(13.69, 22.5) * mm, "mid": v(13.76, 22.93) * mm, "end": v(13.64, 23.36) * mm});
            skArc(sketch, "E305", {"start": v(12.9, 22.42) * mm, "mid": v(13.3, 22.27) * mm, "end": v(13.69, 22.5) * mm});
            skArc(sketch, "E306", {"start": v(12.8, 23.05) * mm, "mid": v(12.74, 22.72) * mm, "end": v(12.9, 22.42) * mm});
            skArc(sketch, "E307", {"start": v(13.3, 23.36) * mm, "mid": v(13.01, 23.27) * mm, "end": v(12.8, 23.05) * mm});
            skArc(sketch, "E308", {"start": v(13.32, 23.66) * mm, "mid": v(12.9, 23.45) * mm, "end": v(12.57, 23.1) * mm});
            skArc(sketch, "E309", {"start": v(12.57, 23.1) * mm, "mid": v(12.52, 22.71) * mm, "end": v(12.67, 22.35) * mm});
            skArc(sketch, "E310", {"start": v(12.67, 22.35) * mm, "mid": v(13, 22.12) * mm, "end": v(13.4, 22.11) * mm});
            skArc(sketch, "E311", {"start": v(12.52, 21.77) * mm, "mid": v(12.99, 21.88) * mm, "end": v(13.4, 22.11) * mm});
            skArc(sketch, "E312", {"start": v(10.19, 22.76) * mm, "mid": v(10.6, 22.06) * mm, "end": v(11.37, 21.8) * mm});
            skArc(sketch, "E313", {"start": v(10.92, 23.75) * mm, "mid": v(10.35, 23.4) * mm, "end": v(10.19, 22.76) * mm});
            skArc(sketch, "E314", {"start": v(12.38, 23.88) * mm, "mid": v(11.64, 23.88) * mm, "end": v(10.92, 23.75) * mm});
            skArc(sketch, "E315", {"start": v(13.32, 23.66) * mm, "mid": v(12.86, 23.82) * mm, "end": v(12.38, 23.88) * mm});
            skArc(sketch, "E316", {"start": v(10.3, 21.91) * mm, "mid": v(11.29, 21.28) * mm, "end": v(12.46, 21.2) * mm});
            skArc(sketch, "E317", {"start": v(9.97, 23.02) * mm, "mid": v(10.04, 22.44) * mm, "end": v(10.3, 21.91) * mm});
            skArc(sketch, "E318", {"start": v(10.51, 24.02) * mm, "mid": v(10.15, 23.57) * mm, "end": v(9.97, 23.02) * mm});
            skArc(sketch, "E319", {"start": v(11.71, 24.52) * mm, "mid": v(11.08, 24.36) * mm, "end": v(10.51, 24.02) * mm});
            skArc(sketch, "E320", {"start": v(13.67, 23.75) * mm, "mid": v(12.8, 24.4) * mm, "end": v(11.71, 24.52) * mm});
            skLineSegment(sketch, "E321", {"start": v(11.37, 21.8) * mm, "end": v(12.52, 21.77) * mm});
            skArc(sketch, "E322", {"start": v(13.67, 23.75) * mm, "mid": v(14.1, 23.91) * mm, "end": v(14.5, 24.18) * mm});
            skArc(sketch, "E323", {"start": v(14.3, 23.38) * mm, "mid": v(14.37, 23.4) * mm, "end": v(14.44, 23.45) * mm});
            skArc(sketch, "E324", {"start": v(14.44, 23.45) * mm, "mid": v(14.68, 23.65) * mm, "end": v(14.83, 23.93) * mm});
            skLineSegment(sketch, "E325", {"start": v(14.83, 23.93) * mm, "end": v(14.83, 24.83) * mm});
            skLineSegment(sketch, "E326", {"start": v(14.83, 24.83) * mm, "end": v(14.59, 24.85) * mm});
            skLineSegment(sketch, "E327", {"start": v(10.64, 27.3) * mm, "end": v(10.89, 27.22) * mm});
            skLineSegment(sketch, "E328", {"start": v(10.89, 27.22) * mm, "end": v(10.74, 26.76) * mm});
            skLineSegment(sketch, "E329", {"start": v(10.74, 26.76) * mm, "end": v(13.04, 25.97) * mm});
            skLineSegment(sketch, "E330", {"start": v(12.99, 25.48) * mm, "end": v(10.8, 26.15) * mm});
            skLineSegment(sketch, "E331", {"start": v(10.55, 26.14) * mm, "end": v(10.37, 25.63) * mm});
            skLineSegment(sketch, "E332", {"start": v(10.37, 25.63) * mm, "end": v(10.1, 25.7) * mm});
            skLineSegment(sketch, "E333", {"start": v(10.86, 28.09) * mm, "end": v(11.12, 28) * mm});
            skLineSegment(sketch, "E334", {"start": v(10.86, 28.09) * mm, "end": v(11.27, 29.4) * mm});
            skLineSegment(sketch, "E335", {"start": v(11.27, 29.4) * mm, "end": v(11.54, 29.33) * mm});
            skLineSegment(sketch, "E336", {"start": v(11.79, 28.75) * mm, "end": v(13.6, 28.2) * mm});
            skLineSegment(sketch, "E337", {"start": v(11.73, 28.46) * mm, "end": v(13.7, 27.85) * mm});
            skArc(sketch, "E338", {"start": v(11.54, 29.33) * mm, "mid": v(11.53, 28.98) * mm, "end": v(11.79, 28.75) * mm});
            skArc(sketch, "E339", {"start": v(11.73, 28.46) * mm, "mid": v(11.31, 28.39) * mm, "end": v(11.12, 28) * mm});
            skArc(sketch, "E340", {"start": v(14.37, 26.92) * mm, "mid": v(14.19, 27.5) * mm, "end": v(13.7, 27.85) * mm});
            skArc(sketch, "E341", {"start": v(13.04, 25.97) * mm, "mid": v(13.64, 25.95) * mm, "end": v(14.15, 26.26) * mm});
            skArc(sketch, "E342", {"start": v(14.15, 26.26) * mm, "mid": v(14.32, 26.57) * mm, "end": v(14.37, 26.92) * mm});
            skArc(sketch, "E343", {"start": v(10.8, 26.15) * mm, "mid": v(10.68, 26.16) * mm, "end": v(10.55, 26.14) * mm});
            skArc(sketch, "E344", {"start": v(12.99, 25.48) * mm, "mid": v(13.39, 25.42) * mm, "end": v(13.79, 25.48) * mm});
            skArc(sketch, "E345", {"start": v(14.64, 26.9) * mm, "mid": v(14.32, 27.7) * mm, "end": v(13.6, 28.2) * mm});
            skArc(sketch, "E346", {"start": v(13.79, 25.48) * mm, "mid": v(14.4, 26.08) * mm, "end": v(14.64, 26.9) * mm});
            skLineSegment(sketch, "E347", {"start": v(11.8, 30.18) * mm, "end": v(12.64, 31.6) * mm});
            skLineSegment(sketch, "E348", {"start": v(12.64, 31.6) * mm, "end": v(12.84, 31.49) * mm});
            skLineSegment(sketch, "E349", {"start": v(12.84, 31.49) * mm, "end": v(12.62, 31.07) * mm});
            skLineSegment(sketch, "E350", {"start": v(12.62, 31.07) * mm, "end": v(15.3, 29.42) * mm});
            skLineSegment(sketch, "E351", {"start": v(11.8, 30.18) * mm, "end": v(11.99, 30.06) * mm});
            skLineSegment(sketch, "E352", {"start": v(11.99, 30.06) * mm, "end": v(12.25, 30.49) * mm});
            skLineSegment(sketch, "E353", {"start": v(12.48, 30.52) * mm, "end": v(15.17, 28.92) * mm});
            skLineSegment(sketch, "E354", {"start": v(15.17, 28.92) * mm, "end": v(15.25, 28.87) * mm});
            skLineSegment(sketch, "E355", {"start": v(15.25, 28.87) * mm, "end": v(15, 28.44) * mm});
            skLineSegment(sketch, "E356", {"start": v(15, 28.44) * mm, "end": v(15.2, 28.32) * mm});
            skLineSegment(sketch, "E357", {"start": v(15.2, 28.32) * mm, "end": v(16.04, 29.75) * mm});
            skLineSegment(sketch, "E358", {"start": v(16.04, 29.75) * mm, "end": v(15.86, 29.87) * mm});
            skLineSegment(sketch, "E359", {"start": v(15.86, 29.87) * mm, "end": v(15.6, 29.42) * mm});
            skArc(sketch, "E360", {"start": v(15.3, 29.42) * mm, "mid": v(15.45, 29.34) * mm, "end": v(15.6, 29.42) * mm});
            skArc(sketch, "E361", {"start": v(12.48, 30.52) * mm, "mid": v(12.36, 30.55) * mm, "end": v(12.25, 30.49) * mm});
            skLineSegment(sketch, "E362", {"start": v(14.2, 33.02) * mm, "end": v(16.47, 30.71) * mm});
            skLineSegment(sketch, "E363", {"start": v(16.47, 30.71) * mm, "end": v(16.12, 30.37) * mm});
            skLineSegment(sketch, "E364", {"start": v(16.12, 30.37) * mm, "end": v(16.33, 30.14) * mm});
            skLineSegment(sketch, "E365", {"start": v(16.33, 30.14) * mm, "end": v(17.5, 31.39) * mm});
            skLineSegment(sketch, "E366", {"start": v(17.5, 31.39) * mm, "end": v(17.3, 31.56) * mm});
            skLineSegment(sketch, "E367", {"start": v(17.3, 31.56) * mm, "end": v(16.99, 31.21) * mm});
            skLineSegment(sketch, "E368", {"start": v(16.71, 31.23) * mm, "end": v(15.7, 32.25) * mm});
            skLineSegment(sketch, "E369", {"start": v(15.7, 32.25) * mm, "end": v(16.11, 32.64) * mm});
            skLineSegment(sketch, "E370", {"start": v(15.52, 32.4) * mm, "end": v(16.06, 32.95) * mm});
            skLineSegment(sketch, "E371", {"start": v(15.52, 32.4) * mm, "end": v(14.43, 33.49) * mm});
            skLineSegment(sketch, "E372", {"start": v(14.43, 33.49) * mm, "end": v(15.07, 34.1) * mm});
            skLineSegment(sketch, "E373", {"start": v(13.96, 33.03) * mm, "end": v(13.59, 32.66) * mm});
            skLineSegment(sketch, "E374", {"start": v(13.59, 32.66) * mm, "end": v(13.44, 32.84) * mm});
            skLineSegment(sketch, "E375", {"start": v(13.44, 32.84) * mm, "end": v(15.04, 34.35) * mm});
            skArc(sketch, "E376", {"start": v(16.06, 32.95) * mm, "mid": v(16.23, 33.25) * mm, "end": v(16.21, 33.59) * mm});
            skArc(sketch, "E377", {"start": v(15.8, 34.1) * mm, "mid": v(15.44, 34.25) * mm, "end": v(15.07, 34.1) * mm});
            skArc(sketch, "E378", {"start": v(16.21, 33.59) * mm, "mid": v(16.04, 33.87) * mm, "end": v(15.8, 34.1) * mm});
            skArc(sketch, "E379", {"start": v(16.3, 32.98) * mm, "mid": v(16.57, 33.42) * mm, "end": v(16.6, 33.93) * mm});
            skArc(sketch, "E380", {"start": v(16.6, 33.93) * mm, "mid": v(16.43, 34.28) * mm, "end": v(16.13, 34.53) * mm});
            skArc(sketch, "E381", {"start": v(15.8, 34.67) * mm, "mid": v(15.4, 34.58) * mm, "end": v(15.04, 34.35) * mm});
            skArc(sketch, "E382", {"start": v(16.13, 34.53) * mm, "mid": v(15.97, 34.6) * mm, "end": v(15.8, 34.67) * mm});
            skArc(sketch, "E383", {"start": v(14.2, 33.02) * mm, "mid": v(14.08, 33.07) * mm, "end": v(13.96, 33.03) * mm});
            skArc(sketch, "E384", {"start": v(16.71, 31.23) * mm, "mid": v(16.85, 31.16) * mm, "end": v(16.99, 31.21) * mm});
            skArc(sketch, "E385", {"start": v(16.99, 32.52) * mm, "mid": v(16.57, 32.74) * mm, "end": v(16.11, 32.64) * mm});
            skArc(sketch, "E386", {"start": v(17.4, 32.87) * mm, "mid": v(16.87, 33.1) * mm, "end": v(16.3, 32.98) * mm});
            skArc(sketch, "E387", {"start": v(17.4, 32.87) * mm, "mid": v(17.67, 32.7) * mm, "end": v(17.95, 32.55) * mm});
            skArc(sketch, "E388", {"start": v(16.99, 32.52) * mm, "mid": v(17.32, 32.24) * mm, "end": v(17.7, 32.01) * mm});
            skArc(sketch, "E389", {"start": v(17.7, 32.01) * mm, "mid": v(18.03, 31.97) * mm, "end": v(18.33, 32.12) * mm});
            skArc(sketch, "E390", {"start": v(18.33, 32.12) * mm, "mid": v(18.49, 32.42) * mm, "end": v(18.43, 32.76) * mm});
            skArc(sketch, "E391", {"start": v(17.95, 32.55) * mm, "mid": v(18.14, 32.52) * mm, "end": v(18.24, 32.69) * mm});
            skArc(sketch, "E392", {"start": v(18.24, 32.69) * mm, "mid": v(18.22, 32.78) * mm, "end": v(18.16, 32.86) * mm});
            skLineSegment(sketch, "E393", {"start": v(17.97, 33.07) * mm, "end": v(18.16, 32.86) * mm});
            skLineSegment(sketch, "E394", {"start": v(17.97, 33.07) * mm, "end": v(18.1, 33.21) * mm});
            skLineSegment(sketch, "E395", {"start": v(18.1, 33.21) * mm, "end": v(18.43, 32.76) * mm});
            skLineSegment(sketch, "E396", {"start": v(19.02, 33.07) * mm, "end": v(19.16, 32.84) * mm});
            skLineSegment(sketch, "E397", {"start": v(19.16, 32.84) * mm, "end": v(21.76, 34.15) * mm});
            skLineSegment(sketch, "E398", {"start": v(21.78, 34.33) * mm, "end": v(21.23, 35.52) * mm});
            skLineSegment(sketch, "E399", {"start": v(21.23, 35.52) * mm, "end": v(21.07, 35.46) * mm});
            skLineSegment(sketch, "E400", {"start": v(19.87, 33.7) * mm, "end": v(19.23, 35) * mm});
            skLineSegment(sketch, "E401", {"start": v(19.23, 35) * mm, "end": v(19.56, 35.16) * mm});
            skLineSegment(sketch, "E402", {"start": v(19.13, 35.21) * mm, "end": v(19.43, 35.4) * mm});
            skLineSegment(sketch, "E403", {"start": v(19.13, 35.21) * mm, "end": v(18.44, 36.56) * mm});
            skLineSegment(sketch, "E404", {"start": v(18.44, 36.56) * mm, "end": v(19.23, 36.99) * mm});
            skLineSegment(sketch, "E405", {"start": v(17.23, 36.28) * mm, "end": v(19.97, 37.59) * mm});
            skLineSegment(sketch, "E406", {"start": v(19.97, 37.59) * mm, "end": v(20.7, 36.48) * mm});
            skLineSegment(sketch, "E407", {"start": v(20.7, 36.48) * mm, "end": v(20.51, 36.36) * mm});
            skLineSegment(sketch, "E408", {"start": v(19.53, 36.26) * mm, "end": v(19.73, 36.38) * mm});
            skLineSegment(sketch, "E409", {"start": v(19.73, 36.38) * mm, "end": v(20.52, 34.77) * mm});
            skLineSegment(sketch, "E410", {"start": v(20.52, 34.77) * mm, "end": v(20.32, 34.66) * mm});
            skLineSegment(sketch, "E411", {"start": v(17.32, 36.02) * mm, "end": v(17.82, 36.23) * mm});
            skLineSegment(sketch, "E412", {"start": v(17.32, 36.02) * mm, "end": v(17.23, 36.28) * mm});
            skLineSegment(sketch, "E413", {"start": v(19.02, 33.07) * mm, "end": v(19.46, 33.31) * mm});
            skLineSegment(sketch, "E414", {"start": v(19.46, 33.31) * mm, "end": v(18.06, 36.15) * mm});
            skArc(sketch, "E415", {"start": v(18.06, 36.15) * mm, "mid": v(17.96, 36.24) * mm, "end": v(17.82, 36.23) * mm});
            skArc(sketch, "E416", {"start": v(19.43, 35.4) * mm, "mid": v(19.68, 35.8) * mm, "end": v(19.53, 36.26) * mm});
            skArc(sketch, "E417", {"start": v(20.32, 34.66) * mm, "mid": v(20.03, 35.04) * mm, "end": v(19.56, 35.16) * mm});
            skArc(sketch, "E418", {"start": v(19.87, 33.7) * mm, "mid": v(20, 33.58) * mm, "end": v(20.16, 33.6) * mm});
            skArc(sketch, "E419", {"start": v(20.16, 33.6) * mm, "mid": v(21.06, 34.3) * mm, "end": v(21.07, 35.46) * mm});
            skArc(sketch, "E420", {"start": v(20.51, 36.36) * mm, "mid": v(19.99, 36.9) * mm, "end": v(19.23, 36.99) * mm});
            skLineSegment(sketch, "E421", {"start": v(10.1, 25.7) * mm, "end": v(10.64, 27.3) * mm});
            skArc(sketch, "E422", {"start": v(21.76, 34.15) * mm, "mid": v(21.8, 34.24) * mm, "end": v(21.78, 34.33) * mm});
            skArc(sketch, "E423", {"start": v(40.07, 16.48) * mm, "mid": v(40.23, 16.46) * mm, "end": v(40.35, 16.57) * mm});
            skArc(sketch, "E424", {"start": v(26, 10.15) * mm, "mid": v(26, 10.15) * mm, "end": v(26, 10.14) * mm});
            skArc(sketch, "E425.trimOffspring", {"start": v(33.92, 43.42) * mm, "mid": v(26.04, 48.95) * mm, "end": v(18.16, 43.43) * mm});
            skLineSegment(sketch, "E426", {"start": v(10.18, 28.17) * mm, "end": v(18.16, 43.43) * mm});
            skLineSegment(sketch, "E427", {"start": v(41.68, 28.1) * mm, "end": v(33.92, 43.42) * mm});
            skArc(sketch, "E428.trimOffspring", {"start": v(39.54, 32.33) * mm, "mid": v(34.3, 37.15) * mm, "end": v(27.51, 39.32) * mm});
            skArc(sketch, "E429.trimOffspring", {"start": v(10.18, 28.17) * mm, "mid": v(9.82, 18.68) * mm, "end": v(14.73, 10.54) * mm});
            skSolve(sketch);
        }
        {
            var Q0;
            Q0=makeQuery(id+"F0.imprint","IMPRINT",FACE,{"disambiguationData":[TD([[makeQuery(id+"F0.imprint","IMPRINT",EDGE,{"derivedFrom":sQuery(id+"F0.wireOp",EDGE,"E105")}),-1.0]])]});
            var Q1;
            Q1=makeQuery(id+"F0.imprint","IMPRINT",FACE,{"disambiguationData":[TD([[makeQuery(id+"F0.imprint","IMPRINT",EDGE,{"derivedFrom":sQuery(id+"F0.wireOp",EDGE,"E122")}),1.0]])]});
            var Q2;
            Q2=makeQuery(id+"F0.imprint","IMPRINT",FACE,{"disambiguationData":[TD([[makeQuery(id+"F0.imprint","IMPRINT",EDGE,{"derivedFrom":sQuery(id+"F0.wireOp",EDGE,"E147")}),1.0]])]});
            var Q3;
            Q3=makeQuery(id+"F0.imprint","IMPRINT",FACE,{"disambiguationData":[TD([[makeQuery(id+"F0.imprint","IMPRINT",EDGE,{"derivedFrom":sQuery(id+"F0.wireOp",EDGE,"E174")}),-1.0]])]});
            var Q4;
            Q4=makeQuery(id+"F0.imprint","IMPRINT",FACE,{"disambiguationData":[TD([[makeQuery(id+"F0.imprint","IMPRINT",EDGE,{"derivedFrom":sQuery(id+"F0.wireOp",EDGE,"E197")}),1.0]])]});
            var Q5;
            Q5=makeQuery(id+"F0.imprint","IMPRINT",FACE,{"disambiguationData":[TD([[makeQuery(id+"F0.imprint","IMPRINT",EDGE,{"derivedFrom":sQuery(id+"F0.wireOp",EDGE,"E211")}),-1.0]])]});
            var Q6;
            Q6=makeQuery(id+"F0.imprint","IMPRINT",FACE,{"disambiguationData":[TD([[makeQuery(id+"F0.imprint","IMPRINT",EDGE,{"derivedFrom":sQuery(id+"F0.wireOp",EDGE,"E81")}),-1.0]])]});
            var Q7;
            Q7=makeQuery(id+"F0.imprint","IMPRINT",FACE,{"disambiguationData":[TD([[makeQuery(id+"F0.imprint","IMPRINT",EDGE,{"derivedFrom":sQuery(id+"F0.wireOp",EDGE,"E59")}),1.0]])]});
            var Q8;
            Q8=makeQuery(id+"F0.imprint","IMPRINT",FACE,{"disambiguationData":[TD([[makeQuery(id+"F0.imprint","IMPRINT",EDGE,{"derivedFrom":sQuery(id+"F0.wireOp",EDGE,"E37")}),1.0]])]});
            var Q9;
            Q9=makeQuery(id+"F0.imprint","IMPRINT",FACE,{"disambiguationData":[TD([[makeQuery(id+"F0.imprint","IMPRINT",EDGE,{"derivedFrom":sQuery(id+"F0.wireOp",EDGE,"E267")}),1.0]])]});
            var Q10;
            Q10=makeQuery(id+"F0.imprint","IMPRINT",FACE,{"disambiguationData":[TD([[makeQuery(id+"F0.imprint","IMPRINT",EDGE,{"derivedFrom":sQuery(id+"F0.wireOp",EDGE,"E281")}),-1.0]])]});
            var Q11;
            Q11=makeQuery(id+"F0.imprint","IMPRINT",FACE,{"disambiguationData":[TD([[makeQuery(id+"F0.imprint","IMPRINT",EDGE,{"derivedFrom":sQuery(id+"F0.wireOp",EDGE,"E301")}),1.0]])]});
            var Q12;
            {var subQ0=sQuery(id+"F0.wireOp",EDGE,"E324");Q12=makeQuery(id+"F0.imprint","IMPRINT",FACE,{"disambiguationData":[TD([[makeQuery(id+"F0.imprint","IMPRINT",EDGE,{"derivedFrom":subQ0}),1.0]])]});}
            var Q13;
            Q13=makeQuery(id+"F0.imprint","IMPRINT",FACE,{"disambiguationData":[TD([[makeQuery(id+"F0.imprint","IMPRINT",EDGE,{"derivedFrom":sQuery(id+"F0.wireOp",EDGE,"E327")}),-1.0]])]});
            var Q14;
            Q14=makeQuery(id+"F0.imprint","IMPRINT",FACE,{"disambiguationData":[TD([[makeQuery(id+"F0.imprint","IMPRINT",EDGE,{"derivedFrom":sQuery(id+"F0.wireOp",EDGE,"E243")}),1.0]])]});
            var Q15;
            Q15=makeQuery(id+"F0.imprint","IMPRINT",FACE,{"disambiguationData":[TD([[makeQuery(id+"F0.imprint","IMPRINT",EDGE,{"derivedFrom":sQuery(id+"F0.wireOp",EDGE,"E396")}),1.0]])]});
            var Q16;
            Q16=makeQuery(id+"F0.imprint","IMPRINT",FACE,{"disambiguationData":[TD([[makeQuery(id+"F0.imprint","IMPRINT",EDGE,{"derivedFrom":sQuery(id+"F0.wireOp",EDGE,"E362")}),1.0]])]});
            var Q17;
            Q17=makeQuery(id+"F0.imprint","IMPRINT",FACE,{"disambiguationData":[TD([[makeQuery(id+"F0.imprint","IMPRINT",EDGE,{"derivedFrom":sQuery(id+"F0.wireOp",EDGE,"E347")}),-1.0]])]});
            extrude(context, id + "F1", {"entities" : qUnion([Q0, Q1, Q2, Q3, Q4, Q5, Q6, Q7, Q8, Q9, Q10, Q11, Q12, Q13, Q14, Q15, Q16, Q17]), "depth" : 7 * mm});
        }
        {
            var Q0;
            Q0=makeQuery(id+"F0.imprint","IMPRINT",FACE,{"disambiguationData":[TD([[makeQuery(id+"F0.imprint","IMPRINT",EDGE,{"derivedFrom":sQuery(id+"F0.wireOp",EDGE,"E0")}),-1.0]])]});
            extrude(context, id + "F2", {"entities" : qUnion([Q0]), "depth" : 10 * mm});
        }
        {
            var Q0;
            {var subQ0=sQuery(id+"F0.wireOp",EDGE,"E324");Q0=makeQuery(id+"F0.imprint","IMPRINT",FACE,{"disambiguationData":[TD([[makeQuery(id+"F0.imprint","IMPRINT",EDGE,{"derivedFrom":subQ0}),-1.0]])]});}
            var Q1;
            {var subQ7=sQuery(id+"F0.wireOp",EDGE,"E35");Q1=makeQuery(id+"F0.imprint","IMPRINT",FACE,{"disambiguationData":[TD([[makeQuery(id+"F0.imprint","IMPRINT",EDGE,{"derivedFrom":subQ7}),1.0]])]});}
            var Q2;
            {var subQ0=sQuery(id+"F0.wireOp",EDGE,"E17");Q2=makeQuery(id+"F0.imprint","IMPRINT",FACE,{"disambiguationData":[TD([[makeQuery(id+"F0.imprint","IMPRINT",EDGE,{"derivedFrom":subQ0}),1.0]])]});}
            var Q3;
            {var subQ0=sQuery(id+"F0.wireOp",EDGE,"E33");Q3=makeQuery(id+"F0.imprint","IMPRINT",FACE,{"disambiguationData":[TD([[makeQuery(id+"F0.imprint","IMPRINT",EDGE,{"derivedFrom":subQ0}),-1.0]])]});}
            var Q4;
            Q4=makeQuery(id+"F0.imprint","IMPRINT",FACE,{"disambiguationData":[TD([[makeQuery(id+"F0.imprint","IMPRINT",EDGE,{"derivedFrom":sQuery(id+"F0.wireOp",EDGE,"E28")}),-1.0]])]});
            var Q5;
            {var subQ0=sQuery(id+"F0.wireOp",EDGE,"E32");Q5=makeQuery(id+"F0.imprint","IMPRINT",FACE,{"disambiguationData":[TD([[makeQuery(id+"F0.imprint","IMPRINT",EDGE,{"derivedFrom":subQ0}),1.0]])]});}
            var Q6;
            {var subQ1=sQuery(id+"F0.wireOp",EDGE,"E31");Q6=makeQuery(id+"F0.imprint","IMPRINT",FACE,{"disambiguationData":[TD([[makeQuery(id+"F0.imprint","IMPRINT",EDGE,{"derivedFrom":subQ1}),1.0]])]});}
            var Q7;
            Q7=makeQuery(id+"F0.imprint","IMPRINT",FACE,{"disambiguationData":[TD([[makeQuery(id+"F0.imprint","IMPRINT",EDGE,{"derivedFrom":sQuery(id+"F0.wireOp",EDGE,"E370")}),1.0]])]});
            var Q8;
            Q8=makeQuery(id+"F0.imprint","IMPRINT",FACE,{"disambiguationData":[TD([[makeQuery(id+"F0.imprint","IMPRINT",EDGE,{"derivedFrom":sQuery(id+"F0.wireOp",EDGE,"E308")}),-1.0]])]});
            var Q9;
            Q9=makeQuery(id+"F0.imprint","IMPRINT",FACE,{"disambiguationData":[TD([[makeQuery(id+"F0.imprint","IMPRINT",EDGE,{"derivedFrom":sQuery(id+"F0.wireOp",EDGE,"E301")}),-1.0]])]});
            var Q10;
            Q10=makeQuery(id+"F0.imprint","IMPRINT",FACE,{"disambiguationData":[TD([[makeQuery(id+"F0.imprint","IMPRINT",EDGE,{"derivedFrom":sQuery(id+"F0.wireOp",EDGE,"E56")}),1.0]])]});
            var Q11;
            Q11=makeQuery(id+"F0.imprint","IMPRINT",FACE,{"disambiguationData":[TD([[makeQuery(id+"F0.imprint","IMPRINT",EDGE,{"derivedFrom":sQuery(id+"F0.wireOp",EDGE,"E182")}),-1.0]])]});
            var Q12;
            Q12=makeQuery(id+"F0.imprint","IMPRINT",FACE,{"disambiguationData":[TD([[makeQuery(id+"F0.imprint","IMPRINT",EDGE,{"derivedFrom":sQuery(id+"F0.wireOp",EDGE,"E215")}),1.0]])]});
            extrude(context, id + "F3", {"entities" : qUnion([Q0, Q1, Q2, Q3, Q4, Q5, Q6, Q7, Q8, Q9, Q10, Q11, Q12]), "depth" : 5 * mm});
        }
        {
            var Q0;
            {var subQ2=sQuery(id+"F0.wireOp",EDGE,"E4");Q0=makeQuery(id+"F0.imprint","IMPRINT",FACE,{"disambiguationData":[TD([[makeQuery(id+"F0.imprint","IMPRINT",EDGE,{"derivedFrom":subQ2}),1.0]])]});}
            extrude(context, id + "F4", {"entities" : qUnion([Q0]), "depth" : 4.5 * mm});
        }
        {
            var Q0;
            Q0=makeQuery(id+"F4.opExtrude","CAP_FACE",FACE,{"disambiguationData":[OSD([sQuery(id+"F0.wireOp",EDGE,"E3"),sQuery(id+"F0.wireOp",EDGE,"E4"),sQuery(id+"F0.wireOp",EDGE,"E5"),sQuery(id+"F0.wireOp",EDGE,"E35"),sQuery(id+"F0.wireOp",EDGE,"E425.trimOffspring"),sQuery(id+"F0.wireOp",EDGE,"E426"),sQuery(id+"F0.wireOp",EDGE,"E427"),sQuery(id+"F0.wireOp",EDGE,"E428.trimOffspring")])],"isStart":false});
            var sketch = newSketch(context, id + "F5", { "sketchPlane" : qUnion([Q0])});
            skLineSegment(sketch, "E430", {"start": v(26.04, 40.93) * mm, "end": v(26.04, 48.95) * mm});
            skPoint(sketch, "E430.endSnap0", {"position": v(26.04, 48.95) * mm});
            skLineSegment(sketch, "E431", {"start": v(26.04, 44.94) * mm, "end": v(27, 44.94) * mm});
            skPoint(sketch, "E431.endSnap0", {"position": v(26.04, 44.94) * mm});
            skSolve(sketch);
        }
        {
            var Q0;
            Q0=sQuery(id+"F5.wireOp",VERTEX,"E431.endSnap0");
            var Q1;
            Q1=makeQuery(id+"F4.opExtrude","SWEPT_BODY",BODY,{"disambiguationData":[OSD([sQuery(id+"F0.wireOp",EDGE,"E3"),sQuery(id+"F0.wireOp",EDGE,"E4"),sQuery(id+"F0.wireOp",EDGE,"E5"),sQuery(id+"F0.wireOp",EDGE,"E35"),sQuery(id+"F0.wireOp",EDGE,"E425.trimOffspring"),sQuery(id+"F0.wireOp",EDGE,"E426"),sQuery(id+"F0.wireOp",EDGE,"E427"),sQuery(id+"F0.wireOp",EDGE,"E428.trimOffspring")])]});
            hole(context, id + "F6", {"style" : HoleStyle.SIMPLE, "endStyle" : HoleEndStyle.THROUGH, "holeDiameter" : 6 * mm, "locations" : qUnion([Q0]), "scope" : qUnion([Q1]), "isTappedThrough" : true});
        }
    });
